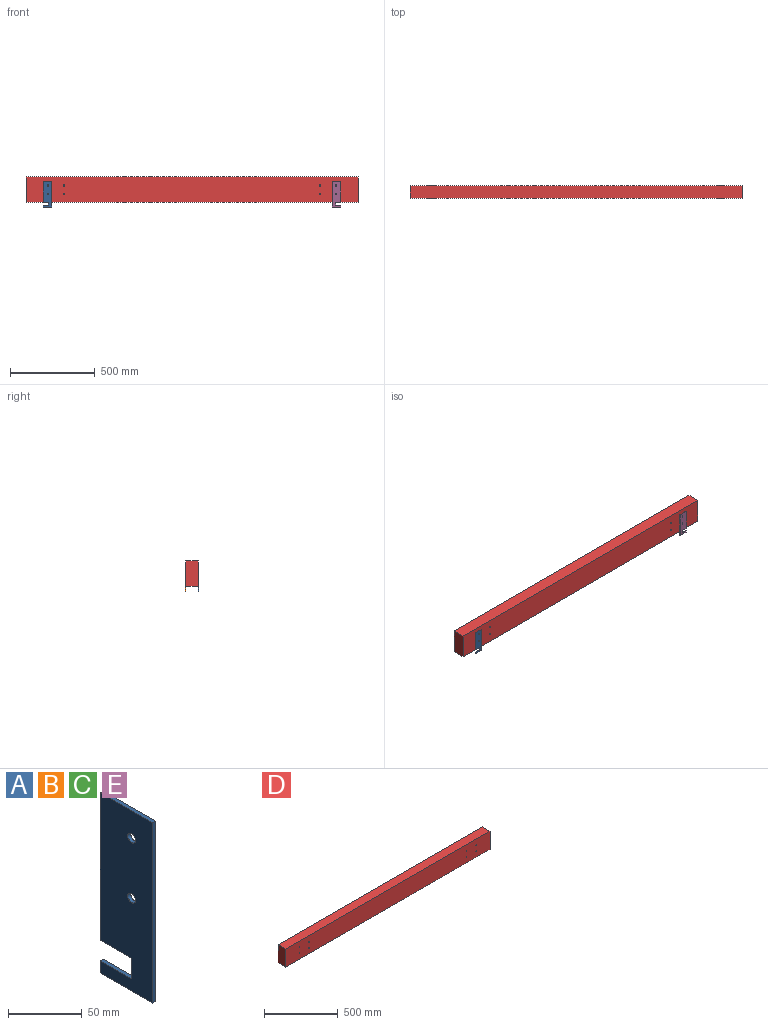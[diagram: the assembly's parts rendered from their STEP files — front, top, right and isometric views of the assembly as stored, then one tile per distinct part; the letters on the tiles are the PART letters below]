
ASSEMBLY  parts=5 mates=4
PART A: 12 faces, bbox 3x50x150 mm
  f0: plane 10x3mm, normal (0,1,0), area 30mm2, adj f1,f8,f10,f11
  f1: plane 30x3mm, normal (0,0,1), area 90mm2, adj f0,f2,f10,f11
  f2: plane 17.3x3mm, normal (0,1,0), area 51.9mm2, adj f1,f3,f10,f11
  f3: plane 30x3mm, normal (0,0,-1), area 90mm2, adj f2,f4,f10,f11
  f4: plane 122.7x3mm, normal (0,1,0), area 368.1mm2, adj f3,f5,f10,f11
  f5: plane 50x3mm, normal (0,0,1), area 150mm2, adj f4,f6,f10,f11
  f6: plane 150x3mm, normal (0,-1,0), area 450mm2, adj f5,f8,f10,f11
  f7: cylinder r=3.75mm len=7.5mm, axis (-1,0,0), area 70.7mm2, adj f10,f11
  f8: plane 50x3mm, normal (0,0,-1), area 150mm2, adj f0,f6,f10,f11
  f9: cylinder r=3.75mm len=7.5mm, axis (-1,0,0), area 70.7mm2, adj f10,f11
  f10: plane 150x50mm, normal (1,0,0), area 6892.6mm2, adj f0,f1,f2,f3,f4,f5,f6,f7
  f11: plane 150x50mm, normal (-1,0,0), area 6892.6mm2, adj f0,f1,f2,f3,f4,f5,f6,f7
PART B: same geometry as A
PART C: same geometry as A
PART D: 14 faces, bbox 1961x75x150 mm
  f0: plane 150x75mm, normal (-1,0,0), area 11250mm2, adj f1,f10,f12,f13
  f1: plane 1961x75mm, normal (0,0,-1), area 147075mm2, adj f0,f2,f12,f13
  f2: plane 150x75mm, normal (1,0,0), area 11250mm2, adj f1,f10,f12,f13
  f3: cylinder r=3.75mm len=75mm, axis (0,1,0), area 1767.1mm2, adj f12,f13
  f4: cylinder r=3.75mm len=75mm, axis (0,1,0), area 1767.1mm2, adj f12,f13
  f5: cylinder r=3.75mm len=75mm, axis (0,1,0), area 1767.1mm2, adj f12,f13
  f6: cylinder r=3.75mm len=75mm, axis (0,1,0), area 1767.1mm2, adj f12,f13
  f7: cylinder r=3.75mm len=75mm, axis (0,1,0), area 1767.1mm2, adj f12,f13
  f8: cylinder r=3.75mm len=75mm, axis (0,1,0), area 1767.1mm2, adj f12,f13
  f9: cylinder r=3.75mm len=75mm, axis (0,1,0), area 1767.1mm2, adj f12,f13
  f10: plane 1961x75mm, normal (0,0,1), area 147075mm2, adj f0,f2,f12,f13
  f11: cylinder r=3.75mm len=75mm, axis (0,1,0), area 1767.1mm2, adj f12,f13
  f12: plane 1961x150mm, normal (0,-1,0), area 293796.6mm2, adj f0,f1,f2,f3,f4,f5,f6,f7
  f13: plane 1961x150mm, normal (0,1,0), area 293796.6mm2, adj f0,f1,f2,f3,f4,f5,f6,f7
PART E: same geometry as A
PLACE A rot(axis=(0,0,1),90deg) t=(151,-78,122.7)mm
PLACE B rot(axis=(0,0,1),90deg) t=(151,0,122.7)mm
PLACE C rot(axis=(0,0,-1),90deg) t=(1810,3,122.7)mm
PLACE D at identity fixed
PLACE E rot(axis=(0,0,-1),90deg) t=(1810,-75,122.7)mm
MATE fastened A.f7 <-> D.f9  axis (0,1,0) through (131,-75,100)mm
MATE fastened B.f7 <-> D.f9  axis (0,-1,0) through (131,0,100)mm
MATE fastened C.f7 <-> D.f7  axis (0,-1,0) through (1830,0,100)mm
MATE fastened E.f7 <-> D.f7  axis (0,1,0) through (1830,-75,100)mm
